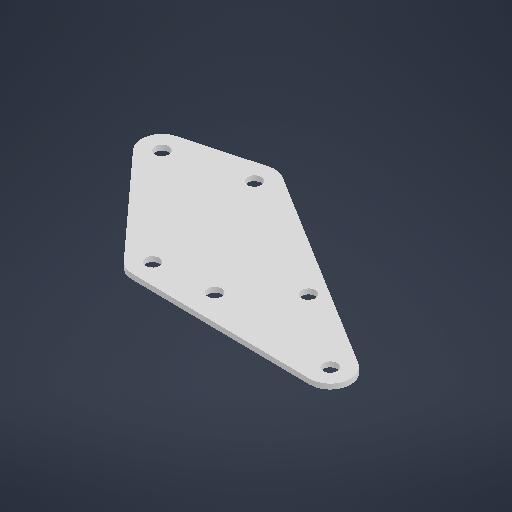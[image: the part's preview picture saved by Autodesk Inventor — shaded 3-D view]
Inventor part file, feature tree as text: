
AUTODESK INVENTOR PART (.ipt)
format: ipt  version: 2025.2 (Build 292293000, 293)  size: 199,680 bytes
history: native  units: in
note: dims shown in document units (in); Inventor stores cm internally (conversion verified against a paired STEP export)
features: extrude x1, sketch x1
ambient origin geometry x8: Origin, YZ Plane, XZ Plane, XY Plane, X Axis, Y Axis, Z Axis, Center Point
bodies: Solid1 (feature_tree)
feature tree (2):
  extrude  "Extrusion1"  Depth=0.0625in
  sketch  "Sketch1"  dims[d0=0.5in d1=0.5in d2=0.5in d8=0.0625in d9=0.0in d10=0.5in]
